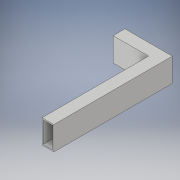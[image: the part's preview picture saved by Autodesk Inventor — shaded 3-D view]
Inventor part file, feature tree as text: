
AUTODESK INVENTOR PART (.ipt)
format: ipt  version: 2018 (Build 220112000, 112)  size: 129,536 bytes
history: native  units: in
note: dims shown in document units (in); Inventor stores cm internally (conversion verified against a paired STEP export)
features: extrude x3, sketch x3
ambient origin geometry x8: Origin, YZ Plane, XZ Plane, XY Plane, X Axis, Y Axis, Z Axis, Center Point
bodies: Body1 (feature_tree)
feature tree (6):
  extrude  "Extrusion12"  Depth=2.0in
  extrude  "Extrusion13"  Depth=0.1in
  extrude  "Extrusion14"  Depth=0.1in
  sketch  "Sketch15"  dims[d46=1.0in d47=2.0in]
  sketch  "Sketch16"  dims[d48=0.1in d49=0.1in]
  sketch  "Sketch17"  dims[d50=0.1in d51=0.1in d52=3.0in d53=0.0in d54=1.0in d55=2.0in d56=0.1in d57=0.1in d58=0.1in d59=0.1in d60=10.0in d61=0.0in d62=0.1in d63=0.0in]
